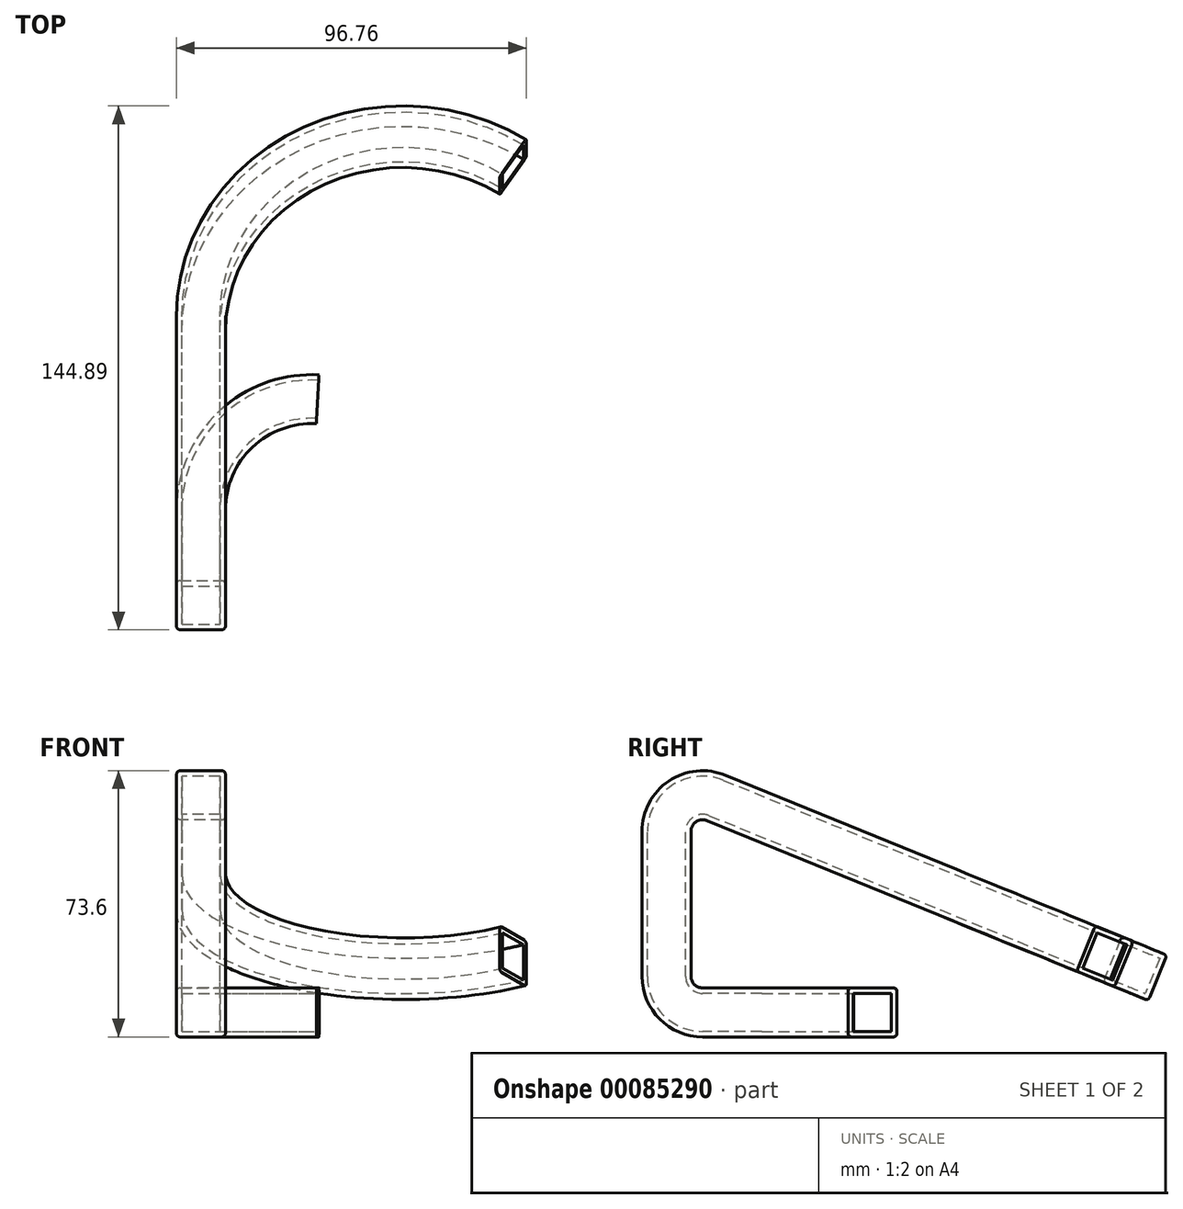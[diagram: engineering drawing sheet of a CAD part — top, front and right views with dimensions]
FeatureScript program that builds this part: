
annotation { "Feature Type Name" : "Feature", "Feature Type Description" : "" }
export const myFeature = defineFeature(function(context is Context, id is Id, definition is map)
    precondition{}
    {
        {
            var Q0;
            Q0=qCreatedBy(makeId("Top.planeOp"),FACE);
            var sketch = newSketch(context, id + "F0", { "sketchPlane" : qUnion([Q0])});
            skArc(sketch, "E0", {"start": v(-30.6, 0) * mm, "mid": v(-21.04, 22.23) * mm, "end": v(1.68, 30.56) * mm});
            skSolve(sketch);
        }
        {
            var Q0;
            Q0=qCreatedBy(makeId("Front.planeOp"),FACE);
            var sketch = newSketch(context, id + "F1", { "sketchPlane" : qUnion([Q0])});
            skLineSegment(sketch, "E1.bottom", {"start": v(-37.38, 6.77) * mm, "end": v(-23.83, 6.77) * mm});
            skLineSegment(sketch, "E1.top", {"start": v(-37.38, -6.77) * mm, "end": v(-23.83, -6.77) * mm});
            skLineSegment(sketch, "E1.left", {"start": v(-37.38, 6.77) * mm, "end": v(-37.38, -6.77) * mm});
            skLineSegment(sketch, "E1.right", {"start": v(-23.83, 6.77) * mm, "end": v(-23.83, -6.77) * mm});
            skPoint(sketch, "E1.middle", {"position": v(-30.6, 0) * mm});
            skLineSegment(sketch, "E2.0", {"start": v(-35.87, 5.27) * mm, "end": v(-25.34, 5.27) * mm});
            skLineSegment(sketch, "E2.1", {"start": v(-35.87, 5.27) * mm, "end": v(-35.87, -5.27) * mm});
            skLineSegment(sketch, "E2.2", {"start": v(-35.87, -5.27) * mm, "end": v(-25.34, -5.27) * mm});
            skLineSegment(sketch, "E2.3", {"start": v(-25.34, 5.27) * mm, "end": v(-25.34, -5.27) * mm});
            skSolve(sketch);
        }
        {
            var Q0;
            Q0=makeQuery(id+"F1.imprint","IMPRINT",FACE,{"disambiguationData":[TD([[makeQuery(id+"F1.imprint","IMPRINT",EDGE,{"derivedFrom":sQuery(id+"F1.wireOp",EDGE,"E1.bottom")}),-1.0]])]});
            var Q1;
            Q1=sQuery(id+"F0.wireOp",EDGE,"E0");
            sweep(context, id + "F2", {"profiles" : qUnion([Q0]), "path" : qUnion([Q1])});
        }
        {
            var Q0;
            Q0=makeQuery(id+"F2.opSweep","SWEPT_EDGE",EDGE,{"disambiguationData":[OSD([sQuery(id+"F0.wireOp",EDGE,"E0"),sQuery(id+"F1.wireOp",EDGE,"E1.bottom"),sQuery(id+"F1.wireOp",EDGE,"E1.left")])]});
            var Q1;
            Q1=makeQuery(id+"F2.opSweep","SWEPT_EDGE",EDGE,{"disambiguationData":[OSD([sQuery(id+"F0.wireOp",EDGE,"E0"),sQuery(id+"F1.wireOp",EDGE,"E1.bottom"),sQuery(id+"F1.wireOp",EDGE,"E1.right")])]});
            var Q2;
            Q2=makeQuery(id+"F2.opSweep","SWEPT_EDGE",EDGE,{"disambiguationData":[OSD([sQuery(id+"F0.wireOp",EDGE,"E0"),sQuery(id+"F1.wireOp",EDGE,"E1.top"),sQuery(id+"F1.wireOp",EDGE,"E1.right")])]});
            var Q3;
            Q3=makeQuery(id+"F2.opSweep","SWEPT_EDGE",EDGE,{"disambiguationData":[OSD([sQuery(id+"F0.wireOp",EDGE,"E0"),sQuery(id+"F1.wireOp",EDGE,"E1.top"),sQuery(id+"F1.wireOp",EDGE,"E1.left")])]});
            fillet(context, id + "F3", {"entities" : qUnion([Q0, Q1, Q2, Q3]), "radius" : 1 * mm, "tangentPropagation" : true, "allowEdgeOverflow" : false});
        }
        {
            var Q0;
            Q0=qCreatedBy(makeId("Right.planeOp"),FACE);
            var Q1;
            Q1=makeQuery(id+"F2.opSweep","CAP_VERTEX",VERTEX,{"disambiguationData":[OSD([sQuery(id+"F0.wireOp",EDGE,"E0"),sQuery(id+"F1.wireOp",EDGE,"E2.0"),sQuery(id+"F1.wireOp",EDGE,"E2.3")])],"isStart":true});
            cPlane(context, id + "F4", {"entities" : qUnion([Q0, Q1]), "cplaneType" : CPlaneType.PLANE_POINT, "offset" : 150 * mm, "width" : 150 * mm, "height" : 150 * mm});
        }
        {
            var Q0;
            Q0=qCreatedBy(id+"F4.planeOp",FACE);
            var sketch = newSketch(context, id + "F5", { "sketchPlane" : qUnion([Q0])});
            skLineSegment(sketch, "E3", {"start": v(0, 0) * mm, "end": v(-16.4, 0) * mm});
            skLineSegment(sketch, "E4", {"start": v(-26.4, 10) * mm, "end": v(-26.4, 50.06) * mm});
            skPoint(sketch, "E5.visualSharp", {"position": v(-26.4, 0) * mm});
            skArc(sketch, "E5.filletArc", {"start": v(-26.4, 10) * mm, "mid": v(-23.47, 2.93) * mm, "end": v(-16.4, 0) * mm});
            skLineSegment(sketch, "E6", {"start": v(-12.62, 59.32) * mm, "end": v(51.45, 33.2) * mm});
            skPoint(sketch, "E7.visualSharp", {"position": v(-26.4, 64.93) * mm});
            skArc(sketch, "E7.filletArc", {"start": v(-12.62, 59.32) * mm, "mid": v(-21.97, 58.36) * mm, "end": v(-26.4, 50.06) * mm});
            skSolve(sketch);
        }
        {
            var Q0;
            Q0=makeQuery(id+"F2.opSweep","CAP_FACE",FACE,{"disambiguationData":[OSD([sQuery(id+"F0.wireOp",VERTEX,"E0.start"),sQuery(id+"F1.wireOp",EDGE,"E1.bottom"),sQuery(id+"F1.wireOp",EDGE,"E1.top"),sQuery(id+"F1.wireOp",EDGE,"E1.left"),sQuery(id+"F1.wireOp",EDGE,"E1.right"),sQuery(id+"F1.wireOp",EDGE,"E2.0"),sQuery(id+"F1.wireOp",EDGE,"E2.1"),sQuery(id+"F1.wireOp",EDGE,"E2.2"),sQuery(id+"F1.wireOp",EDGE,"E2.3")])],"isStart":true});
            var Q1;
            Q1 = qConstructionFilter(qBodyType(qCreatedBy(id + "F5" ,EDGE), BodyType.WIRE), ConstructionObject.NO);
            sweep(context, id + "F6", {"operationType" : NewBodyOperationType.ADD, "profiles" : qUnion([Q0]), "path" : qUnion([Q1])});
        }
        {
            var Q0;
            Q0=makeQuery(id+"F6.opSweep","SWEPT_FACE",FACE,{"disambiguationData":[OSD([sQuery(id+"F0.wireOp",VERTEX,"E0.start"),sQuery(id+"F1.wireOp",EDGE,"E2.0"),sQuery(id+"F5.wireOp",EDGE,"E6")])]});
            var sketch = newSketch(context, id + "F7", { "sketchPlane" : qUnion([Q0])});
            skArc(sketch, "E8", {"start": v(52.82, 77.57) * mm, "mid": v(1.12, 79.58) * mm, "end": v(-25.34, 35.1) * mm});
            skSolve(sketch);
        }
        {
            var Q0;
            Q0=makeQuery(id+"F6.opSweep","CAP_FACE",FACE,{"disambiguationData":[OSD([sQuery(id+"F0.wireOp",VERTEX,"E0.start"),sQuery(id+"F1.wireOp",EDGE,"E1.bottom"),sQuery(id+"F1.wireOp",EDGE,"E1.top"),sQuery(id+"F1.wireOp",EDGE,"E1.left"),sQuery(id+"F1.wireOp",EDGE,"E1.right"),sQuery(id+"F1.wireOp",EDGE,"E2.0"),sQuery(id+"F1.wireOp",EDGE,"E2.1"),sQuery(id+"F1.wireOp",EDGE,"E2.2"),sQuery(id+"F1.wireOp",EDGE,"E2.3"),sQuery(id+"F5.wireOp",VERTEX,"E6.end")])],"isStart":false});
            var Q1;
            Q1 = qConstructionFilter(qBodyType(qCreatedBy(id + "F7" ,EDGE), BodyType.WIRE), ConstructionObject.NO);
            sweep(context, id + "F8", {"operationType" : NewBodyOperationType.ADD, "profiles" : qUnion([Q0]), "path" : qUnion([Q1])});
        }
    });
